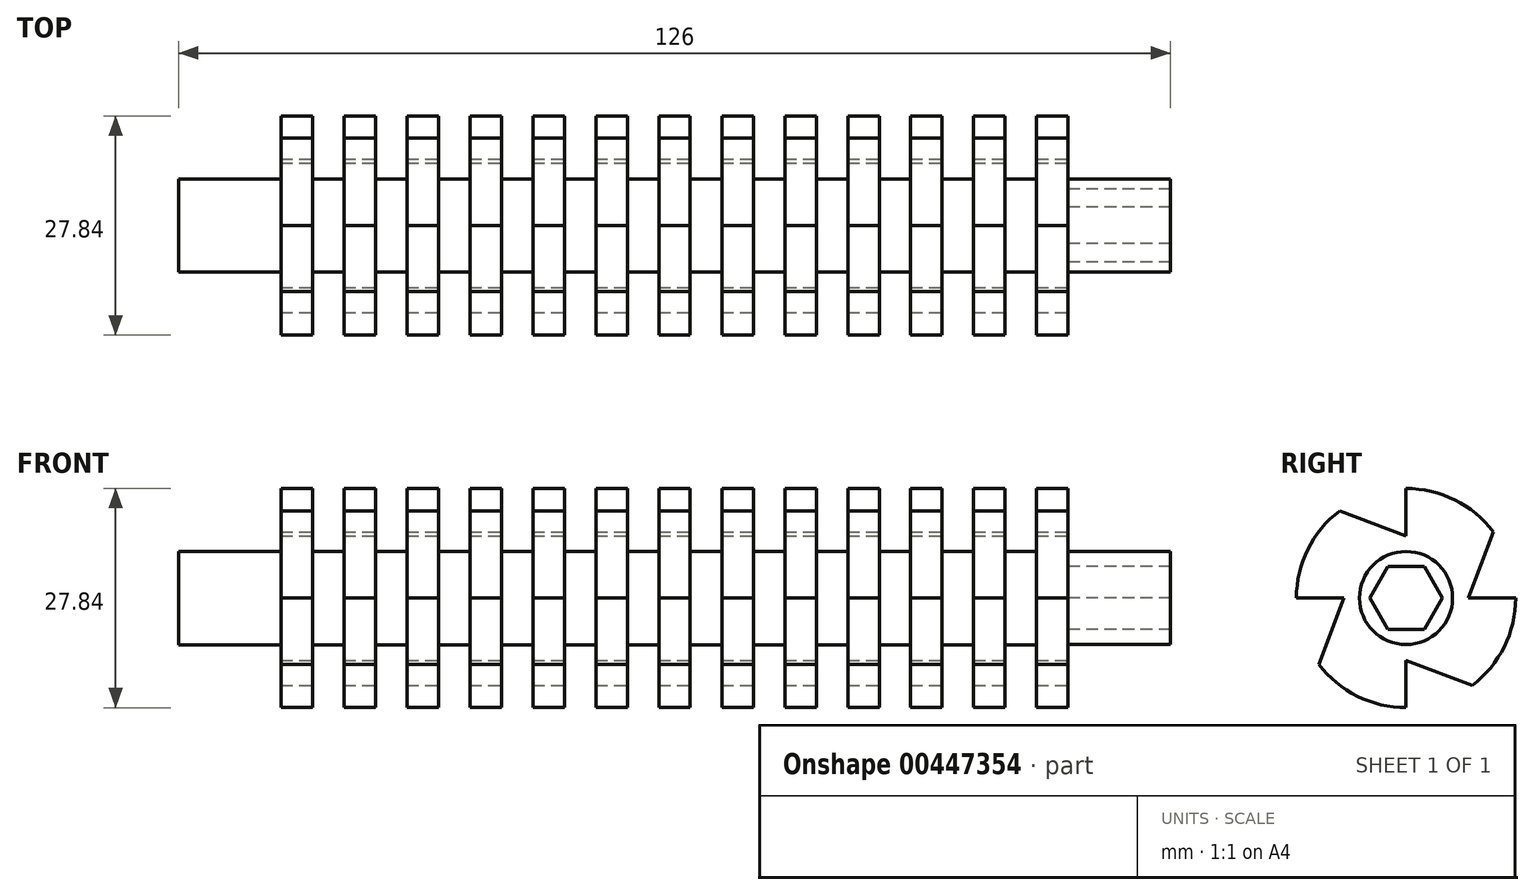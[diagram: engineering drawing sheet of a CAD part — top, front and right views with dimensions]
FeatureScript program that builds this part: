
annotation { "Feature Type Name" : "Feature", "Feature Type Description" : "" }
export const myFeature = defineFeature(function(context is Context, id is Id, definition is map)
    precondition{}
    {
        {
            var Q0;
            Q0=qCreatedBy(makeId("Top.planeOp"),FACE);
            var sketch = newSketch(context, id + "F0", { "sketchPlane" : qUnion([Q0])});
            skLineSegment(sketch, "E0", {"start": v(-41, 0) * mm, "end": v(85, 0) * mm});
            skLineSegment(sketch, "E1", {"start": v(85, 5.91) * mm, "end": v(85, 5.91) * mm});
            skLineSegment(sketch, "E2", {"start": v(85, 5.91) * mm, "end": v(72, 5.91) * mm});
            skLineSegment(sketch, "E3", {"start": v(72, 13.92) * mm, "end": v(72, 5.91) * mm});
            skLineSegment(sketch, "E4", {"start": v(72, 13.92) * mm, "end": v(68, 13.92) * mm});
            skLineSegment(sketch, "E5", {"start": v(68, 5.92) * mm, "end": v(68, 13.92) * mm});
            skLineSegment(sketch, "E6", {"start": v(68, 5.92) * mm, "end": v(64, 5.92) * mm});
            skLineSegment(sketch, "E7", {"start": v(64, 13.92) * mm, "end": v(64, 5.92) * mm});
            skLineSegment(sketch, "E8", {"start": v(64, 13.92) * mm, "end": v(60, 13.92) * mm});
            skLineSegment(sketch, "E9", {"start": v(60, 5.92) * mm, "end": v(60, 13.92) * mm});
            skLineSegment(sketch, "E10", {"start": v(60, 5.92) * mm, "end": v(56, 5.92) * mm});
            skLineSegment(sketch, "E11", {"start": v(56, 13.92) * mm, "end": v(56, 5.92) * mm});
            skLineSegment(sketch, "E12", {"start": v(56, 13.92) * mm, "end": v(52, 13.92) * mm});
            skLineSegment(sketch, "E13", {"start": v(52, 5.92) * mm, "end": v(52, 13.92) * mm});
            skLineSegment(sketch, "E14", {"start": v(52, 5.92) * mm, "end": v(48, 5.92) * mm});
            skLineSegment(sketch, "E15", {"start": v(48, 13.92) * mm, "end": v(48, 5.92) * mm});
            skLineSegment(sketch, "E16", {"start": v(48, 13.92) * mm, "end": v(44, 13.92) * mm});
            skLineSegment(sketch, "E17", {"start": v(44, 5.92) * mm, "end": v(44, 13.92) * mm});
            skLineSegment(sketch, "E18", {"start": v(44, 5.92) * mm, "end": v(40, 5.92) * mm});
            skLineSegment(sketch, "E19", {"start": v(40, 13.92) * mm, "end": v(40, 5.92) * mm});
            skLineSegment(sketch, "E20", {"start": v(4, 5.92) * mm, "end": v(4, 13.92) * mm});
            skLineSegment(sketch, "E21", {"start": v(4, 5.92) * mm, "end": v(0, 5.92) * mm});
            skLineSegment(sketch, "E22", {"start": v(0, 13.92) * mm, "end": v(0, 5.92) * mm});
            skLineSegment(sketch, "E23", {"start": v(0, 13.92) * mm, "end": v(-4, 13.92) * mm});
            skLineSegment(sketch, "E24", {"start": v(-4, 5.92) * mm, "end": v(-4, 13.92) * mm});
            skLineSegment(sketch, "E25", {"start": v(-4, 5.92) * mm, "end": v(-8, 5.92) * mm});
            skLineSegment(sketch, "E26", {"start": v(-8, 13.92) * mm, "end": v(-8, 5.92) * mm});
            skLineSegment(sketch, "E27", {"start": v(-8, 13.92) * mm, "end": v(-12, 13.92) * mm});
            skLineSegment(sketch, "E28", {"start": v(-12, 5.92) * mm, "end": v(-12, 13.92) * mm});
            skLineSegment(sketch, "E29", {"start": v(-12, 5.92) * mm, "end": v(-16, 5.92) * mm});
            skLineSegment(sketch, "E30", {"start": v(-16, 13.92) * mm, "end": v(-16, 5.92) * mm});
            skLineSegment(sketch, "E31", {"start": v(-16, 13.92) * mm, "end": v(-20, 13.92) * mm});
            skLineSegment(sketch, "E32", {"start": v(-20, 5.92) * mm, "end": v(-20, 13.92) * mm});
            skLineSegment(sketch, "E33", {"start": v(-20, 5.92) * mm, "end": v(-24, 5.92) * mm});
            skLineSegment(sketch, "E34", {"start": v(-24, 13.92) * mm, "end": v(-24, 5.92) * mm});
            skLineSegment(sketch, "E35", {"start": v(-24, 13.92) * mm, "end": v(-28, 13.92) * mm});
            skLineSegment(sketch, "E36", {"start": v(-28, 5.92) * mm, "end": v(-28, 13.92) * mm});
            skLineSegment(sketch, "E37", {"start": v(-28, 5.92) * mm, "end": v(-41, 5.92) * mm});
            skLineSegment(sketch, "E38", {"start": v(-41, 5.92) * mm, "end": v(-41, 5.92) * mm});
            skLineSegment(sketch, "E39", {"start": v(-41, 5.92) * mm, "end": v(-41, 0) * mm});
            skLineSegment(sketch, "E40", {"start": v(85, 5.91) * mm, "end": v(85, 0) * mm});
            skLineSegment(sketch, "E41", {"start": v(8, 5.92) * mm, "end": v(8, 13.92) * mm});
            skLineSegment(sketch, "E42", {"start": v(8, 5.92) * mm, "end": v(12, 5.92) * mm});
            skLineSegment(sketch, "E43", {"start": v(12, 13.92) * mm, "end": v(12, 5.92) * mm});
            skLineSegment(sketch, "E44", {"start": v(12, 13.92) * mm, "end": v(16, 13.92) * mm});
            skLineSegment(sketch, "E45", {"start": v(16, 5.92) * mm, "end": v(16, 13.92) * mm});
            skLineSegment(sketch, "E46", {"start": v(16, 5.92) * mm, "end": v(20, 5.92) * mm});
            skLineSegment(sketch, "E47", {"start": v(20, 13.92) * mm, "end": v(20, 5.92) * mm});
            skLineSegment(sketch, "E48", {"start": v(20, 13.92) * mm, "end": v(24, 13.92) * mm});
            skLineSegment(sketch, "E49", {"start": v(24, 5.92) * mm, "end": v(24, 13.92) * mm});
            skLineSegment(sketch, "E50", {"start": v(24, 5.92) * mm, "end": v(28, 5.92) * mm});
            skLineSegment(sketch, "E51", {"start": v(28, 13.92) * mm, "end": v(28, 5.92) * mm});
            skLineSegment(sketch, "E52", {"start": v(28, 13.92) * mm, "end": v(32, 13.92) * mm});
            skLineSegment(sketch, "E53", {"start": v(32, 5.92) * mm, "end": v(32, 13.92) * mm});
            skLineSegment(sketch, "E54", {"start": v(32, 5.92) * mm, "end": v(36, 5.92) * mm});
            skLineSegment(sketch, "E55", {"start": v(36, 13.92) * mm, "end": v(36, 5.92) * mm});
            skLineSegment(sketch, "E56", {"start": v(4, 13.92) * mm, "end": v(8, 13.92) * mm});
            skLineSegment(sketch, "E57", {"start": v(36, 13.92) * mm, "end": v(40, 13.92) * mm});
            skSolve(sketch);
        }
        {
            var Q0;
            Q0=makeQuery(id+"F0.imprint","IMPRINT",FACE,{"disambiguationData":[TD([[makeQuery(id+"F0.imprint","IMPRINT",EDGE,{"derivedFrom":sQuery(id+"F0.wireOp",EDGE,"E0")}),1.0]])]});
            var Q1;
            Q1=sQuery(id+"F0.wireOp",EDGE,"E0");
            revolve(context, id + "F1", {"entities" : qUnion([Q0]), "axis" : qUnion([Q1]), "revolveType" : RevolveType.FULL});
        }
        {
            var Q0;
            Q0=makeQuery(id+"F1.opRevolve","SWEPT_FACE",FACE,{"disambiguationData":[OSD([sQuery(id+"F0.wireOp",EDGE,"E3")])]});
            var sketch = newSketch(context, id + "F2", { "sketchPlane" : qUnion([Q0])});
            skLineSegment(sketch, "E58", {"start": v(0, 13.92) * mm, "end": v(0, 7.92) * mm});
            skLineSegment(sketch, "E59", {"start": v(13.92, 0) * mm, "end": v(7.92, 0) * mm});
            skLineSegment(sketch, "E60", {"start": v(0, -13.92) * mm, "end": v(0, -7.92) * mm});
            skLineSegment(sketch, "E61", {"start": v(-13.92, 0) * mm, "end": v(-7.92, 0) * mm});
            skLineSegment(sketch, "E62", {"start": v(-7.92, 0) * mm, "end": v(-11.08, -8.43) * mm});
            skLineSegment(sketch, "E63", {"start": v(0, -7.92) * mm, "end": v(8.43, -11.08) * mm});
            skLineSegment(sketch, "E64", {"start": v(7.92, 0) * mm, "end": v(11.08, 8.43) * mm});
            skLineSegment(sketch, "E65", {"start": v(0, 7.92) * mm, "end": v(-8.43, 11.08) * mm});
            skCircle(sketch, "E66.cCircle", {"center": v(0, 0) * mm, "radius": 4 * mm, "construction": true});
            skLineSegment(sketch, "E66.0", {"start": v(2.3, -4) * mm, "end": v(-2.3, -4) * mm});
            skLineSegment(sketch, "E66.1", {"start": v(-2.3, -4) * mm, "end": v(-4.62, 0) * mm});
            skLineSegment(sketch, "E66.2", {"start": v(-4.62, 0) * mm, "end": v(-2.3, 4) * mm});
            skLineSegment(sketch, "E66.3", {"start": v(-2.3, 4) * mm, "end": v(2.3, 4) * mm});
            skLineSegment(sketch, "E66.4", {"start": v(2.3, 4) * mm, "end": v(4.62, 0) * mm});
            skLineSegment(sketch, "E66.5", {"start": v(4.62, 0) * mm, "end": v(2.3, -4) * mm});
            skPoint(sketch, "E66.0.midPoint", {"position": v(0, -4) * mm});
            skSolve(sketch);
        }
        {
            var Q0;
            Q0 = qSketchRegion(id + "F2", true);
            extrude(context, id + "F3", {"entities" : qUnion([Q0]), "operationType" : NewBodyOperationType.REMOVE, "depth" : 25 * mm});
        }
        {
            var Q0;
            {var subQ0=sQuery(id+"F2.wireOp",EDGE,"E58");Q0=makeQuery(id+"F2.imprint","IMPRINT",FACE,{"disambiguationData":[TD([[makeQuery(id+"F2.imprint","IMPRINT",EDGE,{"derivedFrom":subQ0}),-1.0]])]});}
            var Q1;
            {var subQ0=sQuery(id+"F2.wireOp",EDGE,"E59");Q1=makeQuery(id+"F2.imprint","IMPRINT",FACE,{"disambiguationData":[TD([[makeQuery(id+"F2.imprint","IMPRINT",EDGE,{"derivedFrom":subQ0}),-1.0]])]});}
            var Q2;
            {var subQ0=sQuery(id+"F2.wireOp",EDGE,"E60");Q2=makeQuery(id+"F2.imprint","IMPRINT",FACE,{"disambiguationData":[TD([[makeQuery(id+"F2.imprint","IMPRINT",EDGE,{"derivedFrom":subQ0}),-1.0]])]});}
            var Q3;
            {var subQ0=sQuery(id+"F2.wireOp",EDGE,"E61");Q3=makeQuery(id+"F2.imprint","IMPRINT",FACE,{"disambiguationData":[TD([[makeQuery(id+"F2.imprint","IMPRINT",EDGE,{"derivedFrom":subQ0}),-1.0]])]});}
            extrude(context, id + "F4", {"entities" : qUnion([Q0, Q1, Q2, Q3]), "operationType" : NewBodyOperationType.REMOVE, "oppositeDirection" : true, "depth" : 250 * mm});
        }
        {
            var Q0;
            Q0 = qSketchRegion(id + "F2", true);
            extrude(context, id + "F5", {"entities" : qUnion([Q0]), "operationType" : NewBodyOperationType.REMOVE, "depth" : 22.8 * mm});
        }
    });
